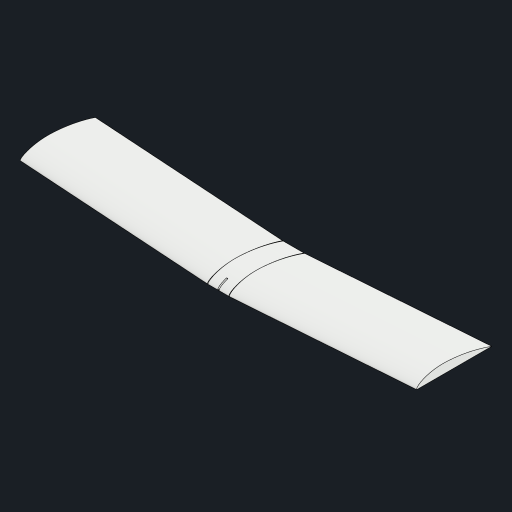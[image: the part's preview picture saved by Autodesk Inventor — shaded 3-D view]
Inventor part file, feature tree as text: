
AUTODESK INVENTOR PART (.ipt)
format: ipt  version: 2023 (Build 270158000, 158)  size: 208,896 bytes
history: native  units: mm
features: sketch x4, extrude x3, other x2, projected_geometry x2, revolve x1, mirror x1
ambient origin geometry x8: Origin, YZ Plane, XZ Plane, XY Plane, X Axis, Y Axis, Z Axis, Center Point
bodies: Body1 (feature_tree)
feature tree (13):
  other  "ソリッド1"
  extrude  "押し出し1"  Depth=25.0mm TaperAngle=0.0deg
  revolve  "回転1"
  extrude  "押し出し3"  Depth=0.698132mm
  mirror  "ミラー4"
  extrude  "押し出し4"  Depth=180.0mm
  sketch  "スケッチ1"
  sketch  "スケッチ7"
  projected_geometry  "投影ループ2"
  sketch  "スケッチ9"
  projected_geometry  "投影ループ4"
  sketch  "スケッチ11"
  other  "断面エッジを投影3"
